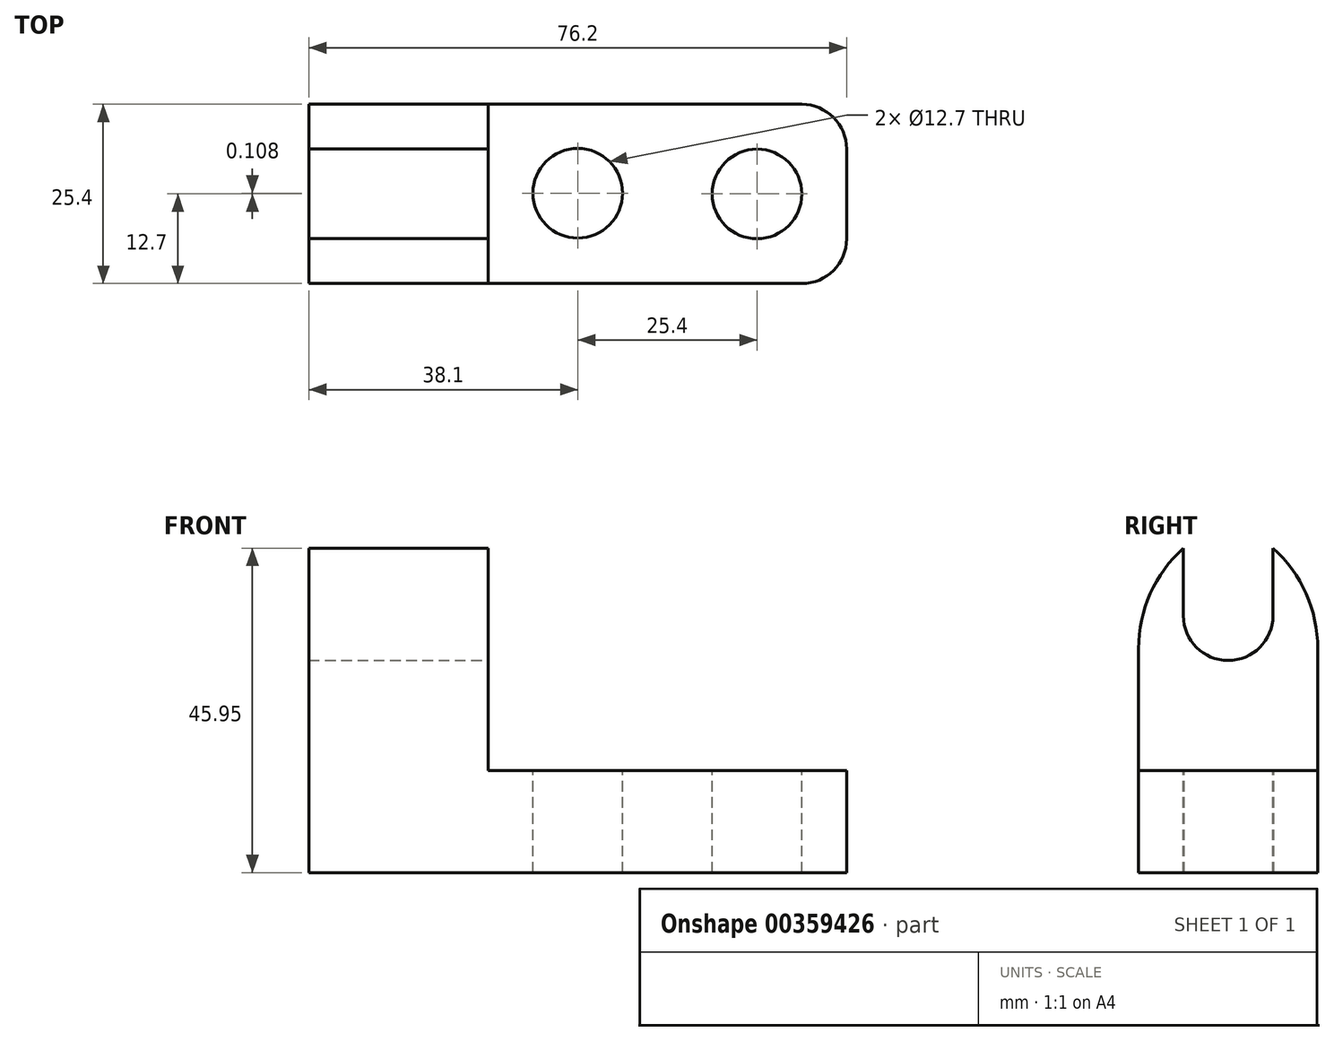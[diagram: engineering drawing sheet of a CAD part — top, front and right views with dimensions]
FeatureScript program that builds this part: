
annotation { "Feature Type Name" : "Feature", "Feature Type Description" : "" }
export const myFeature = defineFeature(function(context is Context, id is Id, definition is map)
    precondition{}
    {
        {
            var Q0;
            Q0=qCreatedBy(makeId("Front.planeOp"),FACE);
            var sketch = newSketch(context, id + "F0", { "sketchPlane" : qUnion([Q0])});
            skLineSegment(sketch, "E0", {"start": v(0, 0) * mm, "end": v(0, 50.8) * mm});
            skLineSegment(sketch, "E1", {"start": v(0, 50.8) * mm, "end": v(25.4, 50.8) * mm});
            skLineSegment(sketch, "E2", {"start": v(25.4, 50.8) * mm, "end": v(25.4, 14.44) * mm});
            skLineSegment(sketch, "E3", {"start": v(25.4, 14.44) * mm, "end": v(76.2, 14.44) * mm});
            skLineSegment(sketch, "E4", {"start": v(76.2, 14.44) * mm, "end": v(76.2, 0) * mm});
            skLineSegment(sketch, "E5", {"start": v(0, 0) * mm, "end": v(76.2, 0) * mm});
            skSolve(sketch);
        }
        {
            var Q0;
            Q0 = qSketchRegion(id + "F0", true);
            extrude(context, id + "F1", {"entities" : qUnion([Q0]), "depth" : 25.4 * mm});
        }
        {
            var Q0;
            Q0=makeQuery(id+"F1.opExtrude","SWEPT_FACE",FACE,{"disambiguationData":[OSD([sQuery(id+"F0.wireOp",EDGE,"E2")])]});
            var sketch = newSketch(context, id + "F2", { "sketchPlane" : qUnion([Q0])});
            skLineSegment(sketch, "E6", {"start": v(-25.4, 14.44) * mm, "end": v(-25.4, 31.75) * mm});
            skLineSegment(sketch, "E7", {"start": v(-19.05, 50.8) * mm, "end": v(-6.35, 50.8) * mm});
            skLineSegment(sketch, "E8", {"start": v(0, 31.75) * mm, "end": v(0, 14.44) * mm});
            skLineSegment(sketch, "E9", {"start": v(0, 14.44) * mm, "end": v(-25.4, 14.44) * mm});
            skPoint(sketch, "E10.visualSharp", {"position": v(-25.4, 50.8) * mm});
            skArc(sketch, "E10.filletArc", {"start": v(-6.35, 50.8) * mm, "mid": v(-19.82, 45.22) * mm, "end": v(-25.4, 31.75) * mm});
            skPoint(sketch, "E11.visualSharp", {"position": v(0, 50.8) * mm});
            skArc(sketch, "E11.filletArc", {"start": v(0, 31.75) * mm, "mid": v(-5.58, 45.22) * mm, "end": v(-19.05, 50.8) * mm});
            skSolve(sketch);
        }
        {
            var Q0;
            {var subQ0=sQuery(id+"F2.wireOp",EDGE,"E10.filletArc");Q0=makeQuery(id+"F2.imprint","IMPRINT",FACE,{"disambiguationData":[TD([[makeQuery(id+"F2.imprint","IMPRINT",EDGE,{"derivedFrom":subQ0}),-1.0]])]});}
            var Q1;
            {var subQ0=sQuery(id+"F2.wireOp",EDGE,"E11.filletArc");Q1=makeQuery(id+"F2.imprint","IMPRINT",FACE,{"disambiguationData":[TD([[makeQuery(id+"F2.imprint","IMPRINT",EDGE,{"derivedFrom":subQ0}),-1.0]])]});}
            var Q2;
            {var subQ0=sQuery(id+"F2.wireOp",EDGE,"E10.filletArc");var subQ4=sQuery(id+"F2.wireOp",EDGE,"E11.filletArc");var subQ5=makeQuery(id+"F2.imprint","INTERSECT",VERTEX,{"derivedFrom":[subQ0,subQ4]});Q2=makeQuery(id+"F2.imprint","IMPRINT",FACE,{"disambiguationData":[TD([[makeQuery(id+"F2.imprint","IMPRINT",EDGE,{"disambiguationData":[TD([[subQ5,-1.0]])],"derivedFrom":subQ0}),-1.0]])]});}
            var Q3;
            {var subQ0=sQuery(id+"F2.wireOp",EDGE,"E10.filletArc");var subQ4=sQuery(id+"F2.wireOp",EDGE,"E11.filletArc");var subQ5=makeQuery(id+"F2.imprint","INTERSECT",VERTEX,{"derivedFrom":[subQ0,subQ4]});Q3=makeQuery(id+"F2.imprint","IMPRINT",FACE,{"disambiguationData":[TD([[makeQuery(id+"F2.imprint","IMPRINT",EDGE,{"disambiguationData":[TD([[subQ5,1.0]])],"derivedFrom":subQ4}),-1.0]])]});}
            extrude(context, id + "F3", {"entities" : qUnion([Q0, Q1, Q2, Q3]), "operationType" : NewBodyOperationType.REMOVE, "oppositeDirection" : true, "depth" : 25.4 * mm});
        }
        {
            var Q0;
            Q0=makeQuery(id+"F1.opExtrude","SWEPT_FACE",FACE,{"disambiguationData":[OSD([sQuery(id+"F0.wireOp",EDGE,"E2")])]});
            var sketch = newSketch(context, id + "F4", { "sketchPlane" : qUnion([Q0])});
            skLineSegment(sketch, "E12", {"start": v(-19.05, 49.1) * mm, "end": v(-19.05, 36.4) * mm});
            skLineSegment(sketch, "E13", {"start": v(-12.7, 30.05) * mm, "end": v(-12.7, 30.05) * mm});
            skLineSegment(sketch, "E14", {"start": v(-6.35, 36.4) * mm, "end": v(-6.35, 49.1) * mm});
            skPoint(sketch, "E15.endSnap0", {"position": v(-12.7, 50.8) * mm});
            skPoint(sketch, "E16.visualSharp", {"position": v(-19.05, 30.05) * mm});
            skArc(sketch, "E16.filletArc", {"start": v(-19.05, 36.4) * mm, "mid": v(-17.2, 31.9) * mm, "end": v(-12.7, 30.05) * mm});
            skPoint(sketch, "E17.visualSharp", {"position": v(-6.35, 30.05) * mm});
            skArc(sketch, "E17.filletArc", {"start": v(-12.7, 30.05) * mm, "mid": v(-8.2, 31.9) * mm, "end": v(-6.35, 36.4) * mm});
            skSolve(sketch);
        }
        {
            var Q0;
            Q0 = qSketchRegion(id + "F4", true);
            var Q1;
            {var subQ1=sQuery(id+"F4.wireOp",EDGE,"E12");Q1=makeQuery(id+"F4.imprint","IMPRINT",FACE,{"disambiguationData":[TD([[makeQuery(id+"F4.imprint","IMPRINT",EDGE,{"derivedFrom":subQ1}),1.0]])]});}
            extrude(context, id + "F5", {"entities" : qUnion([Q0, Q1]), "operationType" : NewBodyOperationType.REMOVE, "oppositeDirection" : true, "depth" : 25.4 * mm});
        }
        {
            var Q0;
            Q0=makeQuery(id+"F1.opExtrude","SWEPT_FACE",FACE,{"disambiguationData":[OSD([sQuery(id+"F0.wireOp",EDGE,"E3")])]});
            var sketch = newSketch(context, id + "F6", { "sketchPlane" : qUnion([Q0])});
            skCircle(sketch, "E18", {"center": v(38.1, -12.6) * mm, "radius": 6.35 * mm});
            skCircle(sketch, "E19", {"center": v(63.5, -12.7) * mm, "radius": 6.35 * mm});
            skSolve(sketch);
        }
        {
            var Q0;
            Q0 = qSketchRegion(id + "F6", true);
            extrude(context, id + "F7", {"entities" : qUnion([Q0]), "operationType" : NewBodyOperationType.REMOVE, "oppositeDirection" : true, "depth" : 25.4 * mm});
        }
        {
            var Q0;
            Q0=makeQuery(id+"F1.opExtrude","SWEPT_FACE",FACE,{"disambiguationData":[OSD([sQuery(id+"F0.wireOp",EDGE,"E3")])]});
            var sketch = newSketch(context, id + "F8", { "sketchPlane" : qUnion([Q0])});
            skLineSegment(sketch, "E20", {"start": v(25.4, 0) * mm, "end": v(69.85, 0) * mm});
            skLineSegment(sketch, "E21", {"start": v(76.2, -6.35) * mm, "end": v(76.2, -19.05) * mm});
            skLineSegment(sketch, "E22", {"start": v(69.85, -25.4) * mm, "end": v(25.4, -25.4) * mm});
            skLineSegment(sketch, "E23", {"start": v(25.4, -25.4) * mm, "end": v(25.4, 0) * mm});
            skPoint(sketch, "E24.visualSharp", {"position": v(76.2, 0) * mm});
            skArc(sketch, "E24.filletArc", {"start": v(76.2, -6.35) * mm, "mid": v(74.34, -1.86) * mm, "end": v(69.85, 0) * mm});
            skPoint(sketch, "E25.visualSharp", {"position": v(76.2, -25.4) * mm});
            skArc(sketch, "E25.filletArc", {"start": v(69.85, -25.4) * mm, "mid": v(74.34, -23.54) * mm, "end": v(76.2, -19.05) * mm});
            skSolve(sketch);
        }
        {
            var Q0;
            Q0=makeQuery(id+"F8.imprint","IMPRINT",FACE,{"disambiguationData":[TD([[makeQuery(id+"F8.imprint","IMPRINT",EDGE,{"derivedFrom":makeQuery(id+"F7.boolean.opBoolean","COPY",EDGE,{"derivedFrom":makeQuery(id+"F7.opExtrude","CAP_EDGE",EDGE,{"disambiguationData":[OSD([sQuery(id+"F6.wireOp",EDGE,"E18")])],"isStart":true})})}),1.0]])]});
            var Q1;
            Q1=makeQuery(id+"F8.imprint","IMPRINT",FACE,{"disambiguationData":[TD([[makeQuery(id+"F8.imprint","IMPRINT",EDGE,{"derivedFrom":makeQuery(id+"F7.boolean.opBoolean","COPY",EDGE,{"derivedFrom":makeQuery(id+"F7.opExtrude","CAP_EDGE",EDGE,{"disambiguationData":[OSD([sQuery(id+"F6.wireOp",EDGE,"E19")])],"isStart":true})})}),1.0]])]});
            var Q2;
            {var subQ0=sQuery(id+"F8.wireOp",EDGE,"E24.filletArc");Q2=makeQuery(id+"F8.imprint","IMPRINT",FACE,{"disambiguationData":[TD([[makeQuery(id+"F8.imprint","IMPRINT",EDGE,{"derivedFrom":subQ0}),-1.0]])]});}
            var Q3;
            {var subQ0=sQuery(id+"F8.wireOp",EDGE,"E25.filletArc");Q3=makeQuery(id+"F8.imprint","IMPRINT",FACE,{"disambiguationData":[TD([[makeQuery(id+"F8.imprint","IMPRINT",EDGE,{"derivedFrom":subQ0}),-1.0]])]});}
            extrude(context, id + "F9", {"entities" : qUnion([Q0, Q1, Q2, Q3]), "operationType" : NewBodyOperationType.REMOVE, "oppositeDirection" : true, "depth" : 25.4 * mm});
        }
    });
